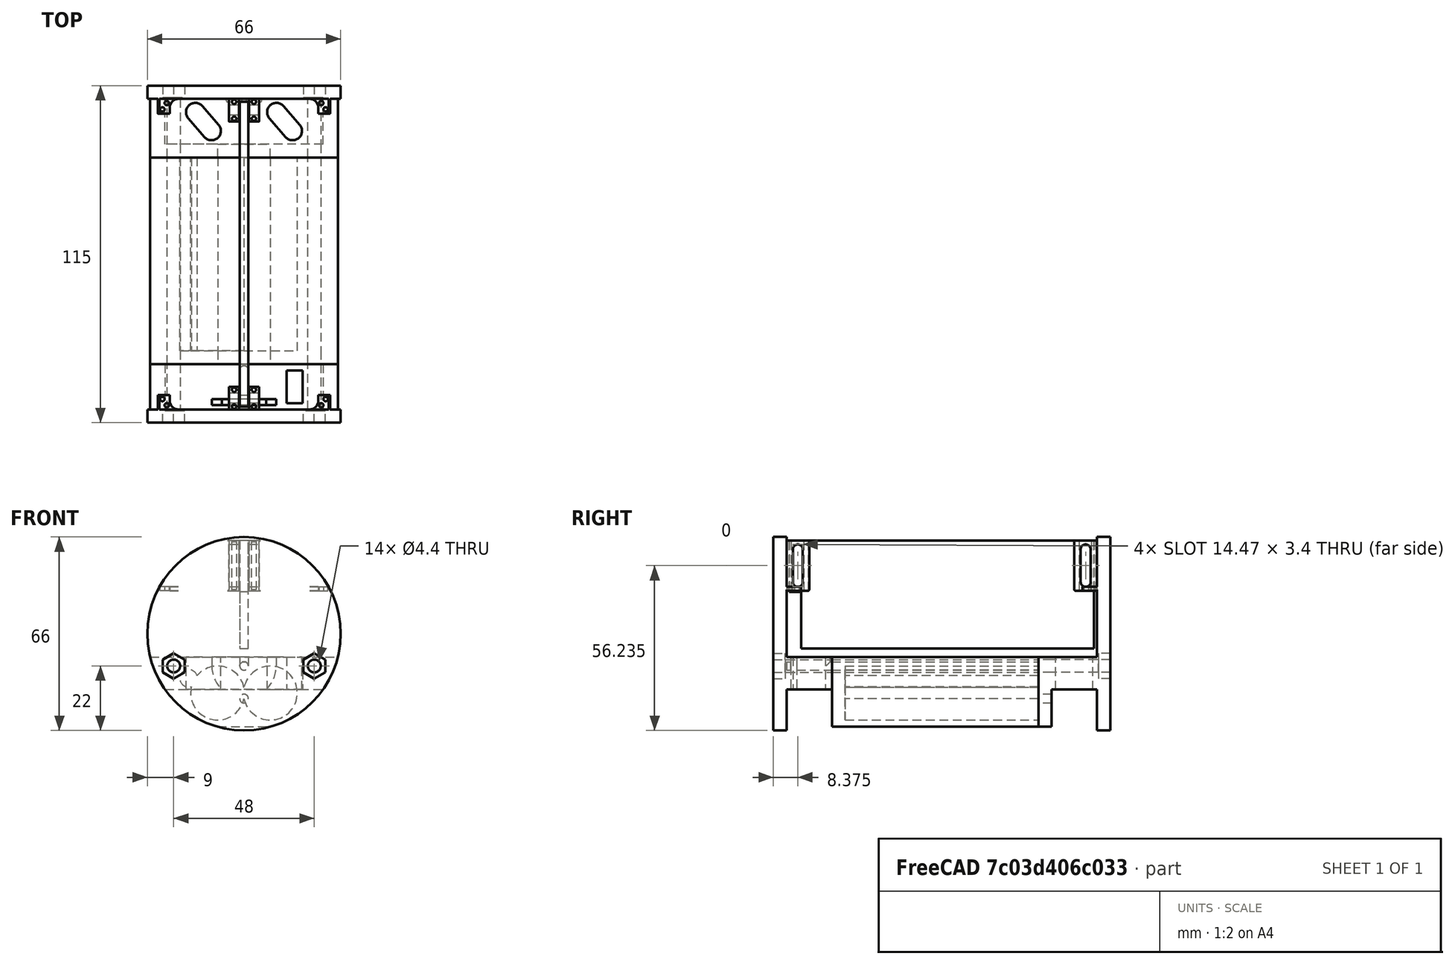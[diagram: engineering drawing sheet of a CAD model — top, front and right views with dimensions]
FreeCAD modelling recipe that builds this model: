
FCSTD DOCUMENT  (FreeCAD 0.19R24276 (Git))
Label: Corte_piezas4
License: Creative Commons Attribution-ShareAlike
LicenseURL: http://creativecommons.org/licenses/by-sa/4.0/
objects: Sketcher::SketchObject×21, PartDesign::Pocket×11, PartDesign::Pad×10, PartDesign::Mirrored×7, PartDesign::Fillet×6, PartDesign::Body×4, PartDesign::ShapeBinder×4, PartDesign::MultiTransform×3, Spreadsheet::Sheet×1, TechDraw::DrawSVGTemplate×1, TechDraw::DrawViewPart×1, TechDraw::DrawViewDimension×1, TechDraw::DrawPage×1
note: 93 computed .brp shape members not serialized (recipe doc carries the construction recipe); baked Part::Feature solids carry a one-line shape summary decoded from their .brp

FEATURE [Spreadsheet::Sheet] Spreadsheet  label="Datos"
  cells = A1=Diámetro pila; B1(DiametroPila)=18; A2=Tolerancia; B2(tolerancia)=0.4; A3=Largo Pila; B3(largoPila)=65; A4=Separacion; B4(separacion)=1; A5=Grosor tapa; B5(grosortapa)=4.5; A6=Largo Bote; B6(LargoBote)=115; A7= Rosca pasante Diámetro; B7(roscaPasante4)=4; A8=Ancho placa electrónica; B8(anchoPlaca)=3; A9=Diámetro tornillos placa; B9(tornillosParaLaPlaca)=3
FEATURE [Sketcher::SketchObject] Sketch  label="habitaculo_pila_antena"
  FullyConstrained = true
  MapMode = 5
  Placement = pos=(0,0,0) rot=(1,0,0;1.5708rad)
  Support = -> [XZ_Plane]
  expr: Constraints[15] = <<Datos>>.DiametroPila
  expr: Constraints[2] = <<Datos>>.DiametroPila + <<Datos>>.tolerancia
  expr: Constraints[7] = <<Datos>>.tolerancia + <<Datos>>.roscaPasante4
  expr: Constraints[19] = 24
  sketch-geometry (13):
    g0: Circle CenterX=0 CenterY=0 CenterZ=0 NormalX=0 NormalY=0 NormalZ=1 AngleXU=0 Radius=33
    g1: LineSegment StartX=-9 StartY=-31.749 StartZ=0 EndX=9 EndY=-31.749 EndZ=0
    g2: LineSegment StartX=-32.0156 StartY=-8 StartZ=0 EndX=32.0156 EndY=-8 EndZ=0
    g3: ArcOfCircle CenterX=-9 CenterY=-20.249 CenterZ=0 NormalX=0 NormalY=0 NormalZ=1 AngleXU=0 Radius=9.2 StartAngle=0.208894 EndAngle=2.4418
    g4: ArcOfCircle CenterX=9 CenterY=-20.249 CenterZ=0 NormalX=0 NormalY=0 NormalZ=1 AngleXU=0 Radius=9.2 StartAngle=3.35049 EndAngle=9.21588
    g5: Circle CenterX=24 CenterY=-11 CenterZ=0 NormalX=0 NormalY=0 NormalZ=1 AngleXU=0 Radius=2.2
    g6: ArcOfCircle CenterX=0 CenterY=0 CenterZ=0 NormalX=0 NormalY=0 NormalZ=1 AngleXU=0 Radius=33 StartAngle=3.38646 EndAngle=4.43616
    g7: ArcOfCircle CenterX=0 CenterY=0 CenterZ=0 NormalX=0 NormalY=0 NormalZ=1 AngleXU=0 Radius=33 StartAngle=4.98862 EndAngle=6.03832
    g8: ArcOfCircle CenterX=-18.8935 CenterY=-15.243 CenterZ=0 NormalX=0 NormalY=0 NormalZ=1 AngleXU=0 Radius=3 StartAngle=0.311443 EndAngle=5.03488
    g9: ArcOfCircle CenterX=-9 CenterY=-20.249 CenterZ=0 NormalX=0 NormalY=0 NormalZ=1 AngleXU=0 Radius=9.2 StartAngle=2.90452 EndAngle=6.07429
    g10: Circle CenterX=-24 CenterY=-11 CenterZ=0 NormalX=0 NormalY=0 NormalZ=1 AngleXU=0 Radius=2.2
    g11: Circle CenterX=0 CenterY=-11 CenterZ=0 NormalX=0 NormalY=0 NormalZ=1 AngleXU=0 Radius=1.45
    g12: LineSegment StartX=24 StartY=-11 StartZ=0 EndX=0 EndY=-11 EndZ=0
  constraints (38):
    c: Diameter(g0) = 66
    c: Horizontal(g1)
    c: Diameter(g3) = 18.4
    c: Equal(g3,g4)
    c: Coincident(g4,g9)
    c: Coincident(g4,g3)
    c: Coincident(g0,g-1)
    c: Diameter(g5) = 4.4
    c: Horizontal(g2)
    c: Vertical(g1,g4)
    c: Coincident(g6,g-1)
    c: Coincident(g6,g1)
    c: Coincident(g7,g6)
    c: Coincident(g7,g1)
    c: Symmetric(g4,g3,g-2)
    c: DistanceX(g3,g4) = 18
    c: PointOnObject(g1,g0)
    c: DistanceY(g1,g3) = 11.5
    c: DistanceY(g5,g2) = 3
    c: DistanceX(g6,g5) = 24
    c: DistanceY(g2,g6) = 8
    c: PointOnObject(g6,g0)
    c: Coincident(g2,g6)
    c: Coincident(g7,g2)
    c: Equal(g3,g9)
    c: Coincident(g3,g8)
    c: Coincident(g9,g8)
    c: Coincident(g3,g9)
    c: Radius(g8) = 3
    c: DistanceX(g8,g2) = -13.1222
    c: DistanceY(g8,g2) = 7.24297
    c: Symmetric(g10,g5,g-2)
    c: Equal(g10,g5)
    c: Diameter(g11) = 2.9  'Antena'
    c: Coincident(g12,g5)
    c: Coincident(g12,g11)
    c: Horizontal(g12)
    c: PointOnObject(g11,g-2)
FEATURE [PartDesign::Pad] Pad  label="habitaculo_Pila"
  Direction = (1,1,1)
  Length = 66
  Length2 = 100
  Midplane = true
  Placement = pos=(0,0,0) rot=(1,0,0;1.5708rad)
  Profile = -> Sketch
  Type = 0
  expr: Length = <<Datos>>.largoPila + <<Datos>>.separacion
FEATURE [Sketcher::SketchObject] Sketch001  label="TapaHabitaculoSK"
  ExternalGeometry = -> [Pad]
  FullyConstrained = true
  MapMode = 5
  Placement = pos=(0,-33,-7.3e-15) rot=(1,0,0;1.5708rad)
  Support = -> [Pad]
  sketch-geometry (7):
    g0: ArcOfCircle CenterX=0 CenterY=-5.4e-15 CenterZ=0 NormalX=0 NormalY=0 NormalZ=1 AngleXU=0 Radius=33 StartAngle=3.38646 EndAngle=4.43616
    g1: ArcOfCircle CenterX=0 CenterY=-5.4e-15 CenterZ=0 NormalX=0 NormalY=0 NormalZ=1 AngleXU=0 Radius=33 StartAngle=4.98862 EndAngle=6.03832
    g2: LineSegment StartX=-32.0156 StartY=-8 StartZ=0 EndX=32.0156 EndY=-8 EndZ=0
    g3: LineSegment StartX=-9 StartY=-31.749 StartZ=0 EndX=9 EndY=-31.749 EndZ=0
    g4: Circle CenterX=-24 CenterY=-11 CenterZ=0 NormalX=0 NormalY=0 NormalZ=1 AngleXU=0 Radius=2.2
    g5: Circle CenterX=0 CenterY=-11 CenterZ=0 NormalX=0 NormalY=0 NormalZ=1 AngleXU=0 Radius=1.45
    g6: Circle CenterX=24 CenterY=-11 CenterZ=0 NormalX=0 NormalY=0 NormalZ=1 AngleXU=0 Radius=2.2
  constraints (15):
    c: Coincident(g0,g-3)
    c: Coincident(g0,g-3)
    c: Coincident(g1,g0)
    c: Coincident(g1,g-4)
    c: Coincident(g1,g-4)
    c: Coincident(g2,g0)
    c: Coincident(g2,g1)
    c: Coincident(g3,g0)
    c: Coincident(g3,g1)
    c: Coincident(g4,g-6)
    c: PointOnObject(g-5,g4)
    c: Coincident(g5,g-7)
    c: Coincident(g6,g-8)
    c: Equal(g6,g-8)
    c: Equal(g5,g-7)
FEATURE [PartDesign::Pad] Pad001  label="TapaHabitaculoPilas"
  BaseFeature = -> Pad
  Direction = (1,1,1)
  Length = 4.5
  Length2 = 100
  Placement = pos=(0,0,0) rot=(1,0,0;1.5708rad)
  Profile = -> Sketch001
  Type = 0
  expr: Length = <<Datos>>.grosortapa
FEATURE [PartDesign::Body] Body  label="Habitaculo_Pila"
  Group = -> [Sketch,Pad,Sketch001,Pad001]
  Origin = -> Origin
  Tip = -> Pad001
FEATURE [PartDesign::ShapeBinder] ShapeBinder  label="LateralA_SB"
  Placement = pos=(0,-4.5,-1e-15) rot=(0,0,1;0rad)
  Support = -> [Pad001]
  TraceSupport = false
FEATURE [Sketcher::SketchObject] Sketch002  label="LateralA_SK"
  ExternalGeometry = -> [ShapeBinder]
  FullyConstrained = true
  MapMode = 5
  Placement = pos=(0,-37.5,-1.19e-14) rot=(1,0,0;1.5708rad)
  Support = -> [ShapeBinder]
  sketch-geometry (9):
    g0: LineSegment StartX=-32.0156 StartY=-8 StartZ=0 EndX=32.0156 EndY=-8 EndZ=0
    g1: LineSegment StartX=-26.96 StartY=-19.0305 StartZ=0 EndX=26.96 EndY=-19.0305 EndZ=0
    g2: ArcOfCircle CenterX=0 CenterY=0 CenterZ=0 NormalX=0 NormalY=0 NormalZ=1 AngleXU=0 Radius=33 StartAngle=3.38646 EndAngle=3.75625
    g3: ArcOfCircle CenterX=0 CenterY=0 CenterZ=0 NormalX=0 NormalY=0 NormalZ=1 AngleXU=0 Radius=33 StartAngle=5.66852 EndAngle=6.03832
    g4: Circle CenterX=24 CenterY=-11 CenterZ=0 NormalX=0 NormalY=0 NormalZ=1 AngleXU=0 Radius=2.2
    g5: Circle CenterX=0 CenterY=-11 CenterZ=0 NormalX=0 NormalY=0 NormalZ=1 AngleXU=0 Radius=1.45
    g6: Circle CenterX=-24 CenterY=-11 CenterZ=0 NormalX=0 NormalY=0 NormalZ=1 AngleXU=0 Radius=2.2
    g7: LineSegment StartX=-32.0156 StartY=-8 StartZ=0 EndX=-24 EndY=-11 EndZ=0
    g8: LineSegment StartX=-24 StartY=-11 StartZ=0 EndX=-26.96 EndY=-19.0305 EndZ=0
  constraints (20):
    c: Coincident(g0,g-3)
    c: Coincident(g0,g-4)
    c: Horizontal(g1)
    c: Coincident(g2,g-1)
    c: Coincident(g2,g0)
    c: Coincident(g2,g1)
    c: Coincident(g3,g2)
    c: Coincident(g3,g0)
    c: Coincident(g3,g1)
    c: Coincident(g4,g-7)
    c: Coincident(g5,g-6)
    c: Coincident(g6,g-5)
    c: Equal(g4,g-7)
    c: Equal(g5,g-6)
    c: Equal(g6,g-5)
    c: Coincident(g7,g0)
    c: Coincident(g7,g6)
    c: Coincident(g8,g1)
    c: Equal(g7,g8)
    c: Coincident(g8,g6)
FEATURE [PartDesign::Pad] Pad002  label="lateralA"
  Direction = (1,1,1)
  Length = 15.5
  Length2 = 100
  Placement = pos=(0,-4.5,-1e-15) rot=(0,0,1;0rad)
  Profile = -> Sketch002
  Type = 0
  expr: Length = <<Datos>>.LargoBote / 2 - 2 * <<Datos>>.grosortapa - (<<Datos>>.largoPila + <<Datos>>.separacion) / 2
FEATURE [Sketcher::SketchObject] Sketch003  label="tapaLateralASK"
  ExternalGeometry = -> [Pad002]
  FullyConstrained = true
  MapMode = 5
  Placement = pos=(0,-53,-3.16e-14) rot=(1,0,0;1.5708rad)
  Support = -> [Pad002]
  sketch-geometry (3):
    g0: Circle CenterX=0 CenterY=0 CenterZ=0 NormalX=0 NormalY=0 NormalZ=1 AngleXU=0 Radius=33
    g1: Circle CenterX=24 CenterY=-11 CenterZ=0 NormalX=0 NormalY=0 NormalZ=1 AngleXU=0 Radius=2.2
    g2: Circle CenterX=-24 CenterY=-11 CenterZ=0 NormalX=0 NormalY=0 NormalZ=1 AngleXU=0 Radius=2.2
  constraints (7):
    c: Coincident(g0,g-1)
    c: PointOnObject(g-3,g0)
    c: Diameter(g-6) = 4.4
    c: Coincident(g1,g-6)
    c: Equal(g1,g-6)
    c: Coincident(g2,g-5)
    c: Equal(g2,g-5)
FEATURE [PartDesign::Pad] Pad003  label="TapaLateralA"
  BaseFeature = -> Pad002
  Direction = (1,1,1)
  Length = 4.5
  Length2 = 100
  Placement = pos=(0,-4.5,-1e-15) rot=(0,0,1;0rad)
  Profile = -> Sketch003
  Type = 0
  expr: Length = <<Datos>>.grosortapa
FEATURE [PartDesign::ShapeBinder] ShapeBinder001  label="LateralB_SB"
  Placement = pos=(0,33,7e-15) rot=(0,0,1;0rad)
  Support = -> [Pad001]
  TraceSupport = false
FEATURE [Sketcher::SketchObject] Sketch004  label="LateralBSK"
  ExternalGeometry = -> [ShapeBinder001]
  FullyConstrained = true
  MapMode = 5
  Placement = pos=(0,33,7e-15) rot=(0,0.707107,0.707107;3.14159rad)
  Support = -> [ShapeBinder001]
  sketch-geometry (6):
    g0: ArcOfCircle CenterX=3.5e-15 CenterY=-2.7e-15 CenterZ=0 NormalX=0 NormalY=0 NormalZ=1 AngleXU=0 Radius=33 StartAngle=3.38646 EndAngle=4.43616
    g1: ArcOfCircle CenterX=3.5e-15 CenterY=-2.7e-15 CenterZ=0 NormalX=0 NormalY=0 NormalZ=1 AngleXU=0 Radius=33 StartAngle=4.98862 EndAngle=6.03832
    g2: LineSegment StartX=-32.0156 StartY=-8 StartZ=0 EndX=32.0156 EndY=-8 EndZ=0
    g3: LineSegment StartX=9 StartY=-31.749 StartZ=0 EndX=-9 EndY=-31.749 EndZ=0
    g4: Circle CenterX=24 CenterY=-11 CenterZ=0 NormalX=0 NormalY=0 NormalZ=1 AngleXU=0 Radius=2.2
    g5: Circle CenterX=-24 CenterY=-11 CenterZ=0 NormalX=0 NormalY=0 NormalZ=1 AngleXU=0 Radius=2.2
  constraints (13):
    c: Coincident(g0,g-3)
    c: Coincident(g1,g0)
    c: Coincident(g1,g-4)
    c: Coincident(g1,g-4)
    c: Coincident(g-3,g0)
    c: Coincident(g2,g0)
    c: Coincident(g2,g1)
    c: Coincident(g3,g1)
    c: Coincident(g3,g0)
    c: Coincident(g4,g-6)
    c: Equal(g4,g-6)
    c: Coincident(g5,g-5)
    c: Equal(g5,g-5)
FEATURE [PartDesign::Pad] Pad004  label="TaparPilaLateralB"
  Direction = (1,1,1)
  Length = 4.5
  Length2 = 100
  Placement = pos=(0,33,7e-15) rot=(0,0,1;0rad)
  Profile = -> Sketch004
  Type = 0
  expr: Length = <<Datos>>.grosortapa
FEATURE [Sketcher::SketchObject] Sketch005  label="LateralBProlongacionSK"
  ExternalGeometry = -> [Pad004]
  FullyConstrained = true
  MapMode = 5
  Placement = pos=(0,37.5,8.5e-15) rot=(0,0.707107,0.707107;3.14159rad)
  Support = -> [Pad004]
  sketch-geometry (8):
    g0: ArcOfCircle CenterX=0 CenterY=0 CenterZ=0 NormalX=0 NormalY=0 NormalZ=1 AngleXU=0 Radius=33 StartAngle=3.38646 EndAngle=3.75625
    g1: ArcOfCircle CenterX=0 CenterY=0 CenterZ=0 NormalX=0 NormalY=0 NormalZ=1 AngleXU=0 Radius=33 StartAngle=5.66852 EndAngle=6.03832
    g2: LineSegment StartX=-26.96 StartY=-19.0305 StartZ=0 EndX=26.96 EndY=-19.0305 EndZ=0
    g3: LineSegment StartX=32.0156 StartY=-8 StartZ=0 EndX=-32.0156 EndY=-8 EndZ=0
    g4: Circle CenterX=-24 CenterY=-11 CenterZ=0 NormalX=0 NormalY=0 NormalZ=1 AngleXU=0 Radius=2.2
    g5: Circle CenterX=24 CenterY=-11 CenterZ=0 NormalX=0 NormalY=0 NormalZ=1 AngleXU=0 Radius=2.2
    g6: LineSegment StartX=-32.0156 StartY=-8 StartZ=0 EndX=-24 EndY=-11 EndZ=0
    g7: LineSegment StartX=-26.96 StartY=-19.0305 StartZ=0 EndX=-24 EndY=-11 EndZ=0
  constraints (18):
    c: Coincident(g0,g-1)
    c: Coincident(g0,g-3)
    c: Coincident(g1,g0)
    c: Coincident(g1,g-4)
    c: Coincident(g2,g0)
    c: Coincident(g2,g1)
    c: Horizontal(g2)
    c: Coincident(g3,g1)
    c: Coincident(g3,g0)
    c: Coincident(g4,g-5)
    c: Coincident(g5,g-6)
    c: Equal(g5,g-6)
    c: Equal(g4,g-5)
    c: Coincident(g6,g0)
    c: Coincident(g6,g4)
    c: Coincident(g7,g0)
    c: Coincident(g7,g4)
    c: Equal(g6,g7)
FEATURE [PartDesign::Pad] Pad005  label="LateralBProlongacion"
  BaseFeature = -> Pad004
  Direction = (1,1,1)
  Length = 15.5
  Length2 = 100
  Placement = pos=(0,33,7e-15) rot=(0,0,1;0rad)
  Profile = -> Sketch005
  Type = 0
  expr: Length = <<lateralA>>.Length
FEATURE [Sketcher::SketchObject] Sketch006  label="TapaLateralB_SK"
  ExternalGeometry = -> [Pad005]
  FullyConstrained = true
  MapMode = 5
  Placement = pos=(0,53,1.96e-14) rot=(0,0.707107,0.707107;3.14159rad)
  Support = -> [Pad005]
  sketch-geometry (3):
    g0: Circle CenterX=0 CenterY=0 CenterZ=0 NormalX=0 NormalY=0 NormalZ=1 AngleXU=0 Radius=33
    g1: Circle CenterX=-24 CenterY=-11 CenterZ=0 NormalX=0 NormalY=0 NormalZ=1 AngleXU=0 Radius=2.2
    g2: Circle CenterX=24 CenterY=-11 CenterZ=0 NormalX=0 NormalY=0 NormalZ=1 AngleXU=0 Radius=2.2
  constraints (6):
    c: Coincident(g0,g-1)
    c: PointOnObject(g-3,g0)
    c: Coincident(g1,g-4)
    c: Coincident(g2,g-6)
    c: Equal(g2,g-6)
    c: Equal(g-4,g1)
FEATURE [PartDesign::Pad] Pad006  label="TapaLateralB"
  BaseFeature = -> Pad005
  Direction = (1,1,1)
  Length = 4.5
  Length2 = 100
  Placement = pos=(0,33,7e-15) rot=(0,0,1;0rad)
  Profile = -> Sketch006
  Type = 0
  expr: Length = <<Datos>>.grosortapa
FEATURE [Sketcher::SketchObject] Sketch007  label="Ranura_AntenaSK"
  ExternalGeometry = -> [Pad003]
  FullyConstrained = true
  MapMode = 5
  Placement = pos=(-1.4e-15,-4.5,-8) rot=(0,0,1;0rad)
  Support = -> [Pad003]
  sketch-geometry (5):
    g0: ArcOfCircle CenterX=0 CenterY=-35 CenterZ=0 NormalX=0 NormalY=0 NormalZ=1 AngleXU=0 Radius=1.45 StartAngle=-1.199e-12 EndAngle=3.14159
    g1: LineSegment StartX=-1.45 StartY=-35 StartZ=0 EndX=-1.45 EndY=-45 EndZ=0
    g2: LineSegment StartX=1.45 StartY=-35 StartZ=0 EndX=1.45 EndY=-45 EndZ=0
    g3: LineSegment StartX=-1.45 StartY=-45 StartZ=0 EndX=1.45 EndY=-45 EndZ=0
    g4: LineSegment StartX=32.0156 StartY=-48.5 StartZ=0 EndX=0 EndY=-33 EndZ=0
  constraints (14):
    c: Tangent(g0,g2) = 1.5708
    c: Tangent(g0,g1) = -1.5708
    c: Vertical(g1)
    c: Coincident(g3,g1)
    c: Coincident(g3,g2)
    c: Horizontal(g3)
    c: Parallel(g2,g1)
    c: Diameter(g0) = 2.9
    c: DistanceY(g2,g2) = 10
    c: Coincident(g4,g-4)
    c: PointOnObject(g4,g-2)
    c: PointOnObject(g4,g-3)
    c: DistanceY(g0,g-3) = 2
    c: PointOnObject(g0,g-2)
FEATURE [PartDesign::Pocket] Pocket  label="ConRanuraAntena"
  BaseFeature = -> Pad003
  Length = 3
  Length2 = 100
  Placement = pos=(0,-4.5,-1e-15) rot=(0,0,1;0rad)
  Profile = -> Sketch007
  Type = 0
FEATURE [Sketcher::SketchObject] Sketch008  label="Con_tuercas_sketch"
  FullyConstrained = false
  MapMode = 5
  Placement = pos=(0,-57.5,-4.07e-14) rot=(1,0,0;1.5708rad)
  Support = -> [Pocket]
  expr: Constraints[19] = 7 + <<Datos>>.tolerancia
  sketch-geometry (16):
    g0: LineSegment StartX=27.7 StartY=-13.1362 StartZ=0 EndX=27.7 EndY=-8.8638 EndZ=0
    g1: LineSegment StartX=27.7 StartY=-8.8638 StartZ=0 EndX=24 EndY=-6.72761 EndZ=0
    g2: LineSegment StartX=24 StartY=-6.72761 StartZ=0 EndX=20.3 EndY=-8.8638 EndZ=0
    g3: LineSegment StartX=20.3 StartY=-8.8638 StartZ=0 EndX=20.3 EndY=-13.1362 EndZ=0
    g4: LineSegment StartX=20.3 StartY=-13.1362 StartZ=0 EndX=24 EndY=-15.2724 EndZ=0
    g5: LineSegment StartX=24 StartY=-15.2724 StartZ=0 EndX=27.7 EndY=-13.1362 EndZ=0
    g6: Circle CenterX=24 CenterY=-11 CenterZ=0 NormalX=0 NormalY=0 NormalZ=1 AngleXU=0 Radius=4.27239
    g7: LineSegment StartX=20.3 StartY=-8.8638 StartZ=0 EndX=27.7 EndY=-8.8638 EndZ=0
    g8: LineSegment StartX=-20.3 StartY=-13.1362 StartZ=0 EndX=-20.3 EndY=-8.8638 EndZ=0
    g9: LineSegment StartX=-20.3 StartY=-8.8638 StartZ=0 EndX=-24 EndY=-6.72761 EndZ=0
    g10: LineSegment StartX=-24 StartY=-6.72761 StartZ=0 EndX=-27.7 EndY=-8.8638 EndZ=0
    g11: LineSegment StartX=-27.7 StartY=-8.8638 StartZ=0 EndX=-27.7 EndY=-13.1362 EndZ=0
    g12: LineSegment StartX=-27.7 StartY=-13.1362 StartZ=0 EndX=-24 EndY=-15.2724 EndZ=0
    g13: LineSegment StartX=-24 StartY=-15.2724 StartZ=0 EndX=-20.3 EndY=-13.1362 EndZ=0
    g14: Circle CenterX=-24 CenterY=-11 CenterZ=0 NormalX=0 NormalY=0 NormalZ=1 AngleXU=0 Radius=4.27239
    g15: LineSegment StartX=-27.7 StartY=-8.8638 StartZ=0 EndX=-20.3 EndY=-8.8638 EndZ=0
  constraints (34):
    c: Coincident(g0,g1)
    c: Coincident(g1,g2)
    c: Coincident(g2,g3)
    c: Coincident(g3,g4)
    c: Coincident(g4,g5)
    c: Coincident(g5,g0)
    c: Equal(g0, g1-g5) x5
    c: PointOnObject(g0,g6)
    c: PointOnObject(g1,g6)
    c: PointOnObject(g2,g6)
    c: PointOnObject(g3,g6)
    c: PointOnObject(g4,g6)
    c: PointOnObject(g5,g6)
    c: Coincident(g7,g2)
    c: Coincident(g7,g0)
    c: Distance(g7) = 7.4
    c: Vertical(g0)
    c: Coincident(g8,g9)
    c: Coincident(g9,g10)
    c: Coincident(g10,g11)
    c: Coincident(g11,g12)
    c: Coincident(g12,g13)
    c: Coincident(g13,g8)
    c: Equal(g8, g9-g13) x5
    c: PointOnObject(g8,g14)
    c: PointOnObject(g9,g14)
    c: PointOnObject(g10,g14)
    c: PointOnObject(g11,g14)
    c: PointOnObject(g12,g14)
    c: PointOnObject(g13,g14)
    c: Coincident(g15,g10)
    c: Coincident(g15,g8)
    c: Distance(g15) = 7.4
    c: Vertical(g8)
FEATURE [PartDesign::Pocket] Pocket001  label="Con_tuercas"
  BaseFeature = -> Pocket
  Length = 4
  Length2 = 100
  Placement = pos=(0,-4.5,-1e-15) rot=(0,0,1;0rad)
  Profile = -> Sketch008
  Type = 0
FEATURE [PartDesign::ShapeBinder] ShapeBinder002  label="SB_Tuercas"
  Placement = pos=(0,-4.5,-1e-15) rot=(0,0,1;0rad)
  Support = -> [Pocket001]
  TraceSupport = false
FEATURE [Sketcher::SketchObject] Sketch009  label="Con_Tuercas"
  ExternalGeometry = -> [ShapeBinder002,Pad006]
  FullyConstrained = true
  MapMode = 5
  Placement = pos=(0,57.5,2.54e-14) rot=(0,0.707107,0.707107;3.14159rad)
  Support = -> [Pad006]
  sketch-geometry (14):
    g0: LineSegment StartX=24 StartY=-6.72761 StartZ=0 EndX=20.3 EndY=-8.8638 EndZ=0
    g1: LineSegment StartX=20.3 StartY=-8.8638 StartZ=0 EndX=20.3 EndY=-13.1362 EndZ=0
    g2: LineSegment StartX=20.3 StartY=-13.1362 StartZ=0 EndX=24 EndY=-15.2724 EndZ=0
    g3: LineSegment StartX=24 StartY=-15.2724 StartZ=0 EndX=27.7 EndY=-13.1362 EndZ=0
    g4: LineSegment StartX=27.7 StartY=-13.1362 StartZ=0 EndX=27.7 EndY=-8.8638 EndZ=0
    g5: LineSegment StartX=27.7 StartY=-8.8638 StartZ=0 EndX=24 EndY=-6.72761 EndZ=0
    g6: Circle CenterX=24 CenterY=-11 CenterZ=0 NormalX=0 NormalY=0 NormalZ=1 AngleXU=0 Radius=4.27239
    g7: LineSegment StartX=-24 StartY=-6.72761 StartZ=0 EndX=-27.7 EndY=-8.8638 EndZ=0
    g8: LineSegment StartX=-27.7 StartY=-8.8638 StartZ=0 EndX=-27.7 EndY=-13.1362 EndZ=0
    g9: LineSegment StartX=-27.7 StartY=-13.1362 StartZ=0 EndX=-24 EndY=-15.2724 EndZ=0
    g10: LineSegment StartX=-24 StartY=-15.2724 StartZ=0 EndX=-20.3 EndY=-13.1362 EndZ=0
    g11: LineSegment StartX=-20.3 StartY=-13.1362 StartZ=0 EndX=-20.3 EndY=-8.8638 EndZ=0
    g12: LineSegment StartX=-20.3 StartY=-8.8638 StartZ=0 EndX=-24 EndY=-6.72761 EndZ=0
    g13: Circle CenterX=-24 CenterY=-11 CenterZ=0 NormalX=0 NormalY=0 NormalZ=1 AngleXU=0 Radius=4.27239
  constraints (30):
    c: Coincident(g0,g1)
    c: Coincident(g1,g2)
    c: Coincident(g2,g3)
    c: Coincident(g3,g4)
    c: Coincident(g4,g5)
    c: Coincident(g5,g0)
    c: Equal(g0, g1-g5) x5
    c: PointOnObject(g0,g6)
    c: PointOnObject(g1,g6)
    c: PointOnObject(g2,g6)
    c: PointOnObject(g3,g6)
    c: PointOnObject(g4,g6)
    c: PointOnObject(g5,g6)
    c: Coincident(g6,g-4)
    c: Coincident(g5,g-3)
    c: Coincident(g7,g8)
    c: Coincident(g8,g9)
    c: Coincident(g9,g10)
    c: Coincident(g10,g11)
    c: Coincident(g11,g12)
    c: Coincident(g12,g7)
    c: Equal(g7, g8-g12) x5
    c: PointOnObject(g7,g13)
    c: PointOnObject(g8,g13)
    c: PointOnObject(g9,g13)
    c: PointOnObject(g10,g13)
    c: PointOnObject(g11,g13)
    c: PointOnObject(g12,g13)
    c: Coincident(g13,g-5)
    c: Coincident(g12,g-6)
FEATURE [PartDesign::Pocket] Pocket002  label="Tapa_lateral_B_con_tuercas"
  BaseFeature = -> Pad006
  Length = 4
  Length2 = 100
  Placement = pos=(0,33,7e-15) rot=(0,0,1;0rad)
  Profile = -> Sketch009
  Type = 0
FEATURE [Sketcher::SketchObject] Sketch010  label="ArandelaSK"
  ExternalGeometry = -> [Pocket001]
  FullyConstrained = true
  MapMode = 5
  Placement = pos=(0,-49.5,-1.09e-14) rot=(0,0.707107,0.707107;3.14159rad)
  Support = -> [Pocket001]
  sketch-geometry (6):
    g0: ArcOfCircle CenterX=0 CenterY=-11 CenterZ=0 NormalX=0 NormalY=0 NormalZ=1 AngleXU=0 Radius=11 StartAngle=3.14159 EndAngle=6.28319
    g1: LineSegment StartX=-11 StartY=0 StartZ=0 EndX=11 EndY=0 EndZ=0
    g2: LineSegment StartX=-11 StartY=0 StartZ=0 EndX=-11 EndY=-11 EndZ=0
    g3: LineSegment StartX=11 StartY=0 StartZ=0 EndX=11 EndY=-11 EndZ=0
    g4: Circle CenterX=0 CenterY=-11 CenterZ=0 NormalX=0 NormalY=0 NormalZ=1 AngleXU=0 Radius=11
    g5: Circle CenterX=0 CenterY=11 CenterZ=0 NormalX=0 NormalY=0 NormalZ=1 AngleXU=0 Radius=11
  constraints (15):
    c: Coincident(g0,g-3)
    c: PointOnObject(g-1,g0)
    c: Horizontal(g1)
    c: PointOnObject(g-1,g1)
    c: Coincident(g2,g1)
    c: Vertical(g3)
    c: Coincident(g1,g3)
    c: Vertical(g2)
    c: Tangent(g0,g2) = -1.5708
    c: Tangent(g0,g3) = 1.5708
    c: Coincident(g4,g0)
    c: PointOnObject(g0,g4)
    c: PointOnObject(g5,g-2)
    c: Equal(g4,g5)
    c: Tangent(g5,g4)
FEATURE [PartDesign::Pocket] Pocket003  label="Arandela_plano_GND"
  BaseFeature = -> Pocket001
  Length = 2
  Length2 = 100
  Placement = pos=(0,-4.5,-1e-15) rot=(0,0,1;0rad)
  Profile = -> Sketch010
  Type = 0
FEATURE [TechDraw::DrawSVGTemplate] Template
  EditableTexts = Designed_by_Name=Designed by Name; Drawing_number=Drawing number; FC-Date=Date; FC-SC=Scale; FC-SH=Sheet; FC-Title=Title; Subtitle=Subtitle; Weight=Weight
  Height = 210
  Orientation = 1
  Width = 297
FEATURE [Sketcher::SketchObject] Sketch011  label="Pasacables_RFM69"
  ExternalGeometry = -> [Pocket003]
  FullyConstrained = true
  MapMode = 5
  Placement = pos=(-1.4e-15,-4.5,-8) rot=(0,0,1;0rad)
  Support = -> [Pocket003]
  sketch-geometry (4):
    g0: LineSegment StartX=14.5156 StartY=-35.2 StartZ=0 EndX=20.0156 EndY=-35.2 EndZ=0
    g1: LineSegment StartX=20.0156 StartY=-35.2 StartZ=0 EndX=20.0156 EndY=-46.3 EndZ=0
    g2: LineSegment StartX=20.0156 StartY=-46.3 StartZ=0 EndX=14.5156 EndY=-46.3 EndZ=0
    g3: LineSegment StartX=14.5156 StartY=-46.3 StartZ=0 EndX=14.5156 EndY=-35.2 EndZ=0
  constraints (12):
    c: Coincident(g0,g1)
    c: Coincident(g1,g2)
    c: Coincident(g2,g3)
    c: Coincident(g3,g0)
    c: Horizontal(g0)
    c: Horizontal(g2)
    c: Vertical(g1)
    c: Vertical(g3)
    c: DistanceX(g0,g-4) = 12
    c: DistanceY(g0,g-4) = 2.2
    c: DistanceY(g-4,g1) = 2.2
    c: DistanceX(g0,g0) = 5.5
FEATURE [PartDesign::Pocket] Pocket004  label="LateralA_Pasacables"
  BaseFeature = -> Pocket003
  Length = 5
  Length2 = 100
  Placement = pos=(0,-4.5,-1e-15) rot=(0,0,1;0rad)
  Profile = -> Sketch011
  Type = 1
FEATURE [Sketcher::SketchObject] Sketch012  label="RanurasPlaca"
  ExternalGeometry = -> [Pocket004]
  FullyConstrained = true
  MapMode = 5
  Placement = pos=(0,-53,-3.74e-14) rot=(0,0.707107,0.707107;3.14159rad)
  Support = -> [Pocket004]
  expr: Constraints[42] = 2 * <<Datos>>.tolerancia
  expr: Constraints[28] = 2 * <<Datos>>.tolerancia
  expr: Constraints[19] = <<Datos>>.anchoPlaca + <<Datos>>.tolerancia
  sketch-geometry (16):
    g0: LineSegment StartX=-5.1 StartY=31.7936 StartZ=0 EndX=-1.7 EndY=31.7936 EndZ=0
    g1: LineSegment StartX=-1.7 StartY=31.7936 StartZ=0 EndX=-1.7 EndY=14.677 EndZ=0
    g2: LineSegment StartX=-1.7 StartY=14.677 StartZ=0 EndX=-5.1 EndY=14.677 EndZ=0
    g3: LineSegment StartX=-5.1 StartY=14.677 StartZ=0 EndX=-5.1 EndY=31.7936 EndZ=0
    g4: LineSegment StartX=1.7 StartY=31.7936 StartZ=0 EndX=5.1 EndY=31.7936 EndZ=0
    g5: LineSegment StartX=5.1 StartY=31.7936 StartZ=0 EndX=5.1 EndY=14.677 EndZ=0
    g6: LineSegment StartX=5.1 StartY=14.677 StartZ=0 EndX=1.7 EndY=14.677 EndZ=0
    g7: LineSegment StartX=1.7 StartY=14.677 StartZ=0 EndX=1.7 EndY=31.7936 EndZ=0
    g8: LineSegment StartX=-1.7 StartY=31.7936 StartZ=0 EndX=1.7 EndY=31.7936 EndZ=0
    g9: LineSegment StartX=5.1 StartY=-8 StartZ=0 EndX=5.1 EndY=14.677 EndZ=0
    g10: LineSegment StartX=0 StartY=0 StartZ=0 EndX=5.22671 EndY=32.5835 EndZ=0
    g11: GeomPoint X=0 Y=3.00003 Z=0
    g12: Circle CenterX=0 CenterY=-10.9733 CenterZ=0 NormalX=0 NormalY=0 NormalZ=1 AngleXU=0 Radius=11
    g13: Circle CenterX=0 CenterY=3.00003 CenterZ=0 NormalX=0 NormalY=0 NormalZ=1 AngleXU=0 Radius=11
    g14: Circle CenterX=0 CenterY=3.00003 CenterZ=0 NormalX=0 NormalY=0 NormalZ=1 AngleXU=0 Radius=11.8
    g15: LineSegment StartX=0 StartY=14.0001 StartZ=0 EndX=0 EndY=14.8001 EndZ=0
  constraints (44):
    c: Coincident(g0,g1)
    c: Coincident(g1,g2)
    c: Coincident(g2,g3)
    c: Coincident(g3,g0)
    c: Horizontal(g0)
    c: Horizontal(g2)
    c: Vertical(g1)
    c: Vertical(g3)
    c: Coincident(g4,g5)
    c: Coincident(g5,g6)
    c: Coincident(g6,g7)
    c: Coincident(g7,g4)
    c: Horizontal(g4)
    c: Horizontal(g6)
    c: Vertical(g5)
    c: Vertical(g7)
    c: Symmetric(g4,g0,g-2)
    c: Equal(g7,g1)
    c: Equal(g6,g2)
    c: DistanceX(g0,g4) = 3.4
    c: Coincident(g8,g0)
    c: Coincident(g8,g4)
    c: PointOnObject(g9,g-3)
    c: Coincident(g9,g5)
    c: Vertical(g9)
    c: Coincident(g10,g-1)
    c: PointOnObject(g10,g-4)
    c: PointOnObject(g4,g10)
    c: Distance(g4,g10) = 0.8
    c: Equal(g8,g4)
    c: PointOnObject(g11,g-2)
    c: PointOnObject(g-5,g12)
    c: PointOnObject(g12,g-2)
    c: PointOnObject(g-6,g12)
    c: Coincident(g13,g11)
    c: Tangent(g13,g-3)
    c: Equal(g13,g12)
    c: Coincident(g14,g11)
    c: PointOnObject(g15,g13)
    c: PointOnObject(g15,g14)
    c: PointOnObject(g15,g-2)
    c: PointOnObject(g15,g-2)
    c: DistanceY(g15,g15) = 0.8
    c: PointOnObject(g6,g14)
FEATURE [PartDesign::Pad] Pad007  label="Ranura_Placa"
  BaseFeature = -> Pocket004
  Direction = (1,1,1)
  Length = 7.75
  Length2 = 100
  Placement = pos=(0,-4.5,-1e-15) rot=(0,0,1;0rad)
  Profile = -> Sketch012
  Type = 0
  expr: Length = <<lateralA>>.Length / 2
FEATURE [Sketcher::SketchObject] Sketch015  label="Agujero_cables_positivo_negativo"
  ExternalGeometry = -> [ShapeBinder001]
  FullyConstrained = true
  MapMode = 5
  Placement = pos=(0,33,7e-15) rot=(1,0,0;1.5708rad)
  Support = -> [Pocket002]
  sketch-geometry (1):
    g0: Circle CenterX=0 CenterY=-22.1569 CenterZ=0 NormalX=0 NormalY=0 NormalZ=1 AngleXU=0 Radius=1.5
  constraints (2):
    c: Coincident(g0,g-3)
    c: Radius(g0) = 1.5
FEATURE [PartDesign::Pocket] Pocket007  label="Agujero_sacar_cables"
  BaseFeature = -> Pocket002
  Length = 5
  Length2 = 100
  Placement = pos=(0,33,7e-15) rot=(0,0,1;0rad)
  Profile = -> Sketch015
  Type = 2
FEATURE [Sketcher::SketchObject] Sketch013  label="SoporteTornilloPlaca"
  ExternalGeometry = -> [Pad007]
  FullyConstrained = true
  MapMode = 5
  Placement = pos=(5.1,-4.5,-1e-15) rot=(0.57735,0.57735,0.57735;2.0944rad)
  Support = -> [Pad007]
  expr: Constraints[10] = <<Datos>>.tornillosParaLaPlaca + <<Datos>>.tolerancia
  sketch-geometry (8):
    g0: ArcOfCircle CenterX=-44.625 CenterY=28.7693 CenterZ=0 NormalX=0 NormalY=0 NormalZ=1 AngleXU=0 Radius=1.7 StartAngle=8e-16 EndAngle=3.14159
    g1: ArcOfCircle CenterX=-44.625 CenterY=17.7012 CenterZ=0 NormalX=0 NormalY=0 NormalZ=1 AngleXU=0 Radius=1.7 StartAngle=3.14159 EndAngle=6.28319
    g2: LineSegment StartX=-46.325 StartY=28.7693 StartZ=0 EndX=-46.325 EndY=17.7012 EndZ=0
    g3: LineSegment StartX=-42.925 StartY=28.7693 StartZ=0 EndX=-42.925 EndY=17.7012 EndZ=0
    g4: LineSegment StartX=-44.625 StartY=31.7936 StartZ=0 EndX=-44.625 EndY=14.677 EndZ=0
    g5: LineSegment StartX=-44.625 StartY=23.2353 StartZ=0 EndX=-40.75 EndY=23.2353 EndZ=0
    g6: LineSegment StartX=-44.625 StartY=28.7693 StartZ=0 EndX=-40.75 EndY=23.2353 EndZ=0
    g7: LineSegment StartX=-40.75 StartY=23.2353 StartZ=0 EndX=-44.625 EndY=17.7012 EndZ=0
  constraints (20):
    c: Tangent(g0,g3) = 1.5708
    c: Tangent(g0,g2) = -1.5708
    c: Tangent(g2,g1) = -1.5708
    c: Tangent(g3,g1) = 1.5708
    c: Vertical(g2)
    c: Equal(g0,g1)
    c: PointOnObject(g4,g-5)
    c: Symmetric(g-3,g-4,g4)
    c: Vertical(g4)
    c: PointOnObject(g0,g4)
    c: Diameter(g0) = 3.4
    c: PointOnObject(g5,g4)
    c: Horizontal(g5)
    c: Symmetric(g-4,g-5,g5)
    c: Coincident(g6,g0)
    c: Coincident(g6,g5)
    c: Coincident(g7,g5)
    c: Coincident(g7,g1)
    c: Angle(g4,g6) = 0.610865
    c: Angle(g7,g4) = 0.610865
FEATURE [PartDesign::Pocket] Pocket005  label="Tornillos_placa"
  BaseFeature = -> Pad007
  Length = 5
  Length2 = 100
  Placement = pos=(0,-4.5,-1e-15) rot=(0,0,1;0rad)
  Profile = -> Sketch013
  Type = 1
FEATURE [Sketcher::SketchObject] Sketch017  label="Ranuras_A_paracaidas"
  ExternalGeometry = -> [Pocket005]
  FullyConstrained = true
  MapMode = 5
  Placement = pos=(0,-4.5,31.7936) rot=(0,0,1;0rad)
  Support = -> [Pocket005]
  sketch-geometry (12):
    g0: Circle CenterX=-3.36795 CenterY=-41.75 CenterZ=0 NormalX=0 NormalY=0 NormalZ=1 AngleXU=0 Radius=0.75
    g1: Circle CenterX=3.36795 CenterY=-41.75 CenterZ=0 NormalX=0 NormalY=0 NormalZ=1 AngleXU=0 Radius=0.75
    g2: Circle CenterX=-3.36795 CenterY=-47.5 CenterZ=0 NormalX=0 NormalY=0 NormalZ=1 AngleXU=0 Radius=0.75
    g3: Circle CenterX=3.36795 CenterY=-47.5 CenterZ=0 NormalX=0 NormalY=0 NormalZ=1 AngleXU=0 Radius=0.75
    g4: LineSegment StartX=-3.36795 StartY=-41.75 StartZ=0 EndX=3.36795 EndY=-41.75 EndZ=0
    g5: LineSegment StartX=3.36795 StartY=-41.75 StartZ=0 EndX=3.36795 EndY=-47.5 EndZ=0
    g6: LineSegment StartX=3.36795 StartY=-47.5 StartZ=0 EndX=-3.36795 EndY=-47.5 EndZ=0
    g7: LineSegment StartX=-3.36795 StartY=-47.5 StartZ=0 EndX=-3.36795 EndY=-41.75 EndZ=0
    g8: LineSegment StartX=3.36795 StartY=-41.75 StartZ=0 EndX=5.1 EndY=-40.75 EndZ=0
    g9: LineSegment StartX=-3.36795 StartY=-41.75 StartZ=0 EndX=-5.1 EndY=-40.75 EndZ=0
    g10: LineSegment StartX=-3.36795 StartY=-47.5 StartZ=0 EndX=-5.1 EndY=-48.5 EndZ=0
    g11: LineSegment StartX=3.36795 StartY=-47.5 StartZ=0 EndX=5.1 EndY=-48.5 EndZ=0
  constraints (27):
    c: Coincident(g4,g5)
    c: Coincident(g5,g6)
    c: Coincident(g6,g7)
    c: Coincident(g7,g4)
    c: Horizontal(g6)
    c: Vertical(g5)
    c: Symmetric(g4,g4,g-2)
    c: Coincident(g8,g4)
    c: Coincident(g8,g-6)
    c: Coincident(g9,g4)
    c: Coincident(g9,g-5)
    c: Coincident(g10,g6)
    c: Coincident(g10,g-5)
    c: Coincident(g11,g5)
    c: Coincident(g11,g-6)
    c: Equal(g8,g11)
    c: Equal(g11,g10)
    c: Coincident(g1,g4)
    c: Coincident(g0,g4)
    c: Coincident(g2,g6)
    c: Coincident(g3,g5)
    c: Equal(g0,g1)
    c: Equal(g1,g3)
    c: Equal(g3,g2)
    c: Diameter(g0) = 1.5
    c: Angle(g4,g9) = 2.61799
    c: Distance(g8) = 2
FEATURE [PartDesign::Pocket] Pocket008  label="Agujeros_paracaidas"
  BaseFeature = -> Pocket005
  Length = 0
  Length2 = 100
  Placement = pos=(0,-4.5,-1e-15) rot=(0,0,1;0rad)
  Profile = -> Sketch017
  Type = 3
  UpToFace = -> Pocket005 [Face32]
FEATURE [Sketcher::SketchObject] Sketch019  label="SK_Agujeros_paracaidas_2"
  ExternalGeometry = -> [Pocket008]
  FullyConstrained = true
  MapMode = 5
  Placement = pos=(0,-53,-3.74e-14) rot=(0,0.707107,0.707107;3.14159rad)
  Support = -> [Pocket008]
  expr: Constraints[6] = 2 * 1.5 + 3 * <<Datos>>.tolerancia
  sketch-geometry (6):
    g0: LineSegment StartX=5.1 StartY=14.677 StartZ=0 EndX=29.5565 EndY=14.677 EndZ=0
    g1: ArcOfCircle CenterX=0 CenterY=0 CenterZ=0 NormalX=0 NormalY=0 NormalZ=1 AngleXU=0 Radius=33 StartAngle=0.473254 EndAngle=0.506517
    g2: LineSegment StartX=25.3565 StartY=16.0094 StartZ=0 EndX=25.3565 EndY=14.677 EndZ=0
    g3: LineSegment StartX=25.3565 StartY=14.677 StartZ=0 EndX=29.1504 EndY=14.677 EndZ=0
    g4: ArcOfCircle CenterX=29.1504 CenterY=14.927 CenterZ=0 NormalX=0 NormalY=0 NormalZ=1 AngleXU=0 Radius=0.25 StartAngle=4.71239 EndAngle=6.75644
    g5: LineSegment StartX=25.3565 StartY=16.0094 StartZ=0 EndX=28.8565 EndY=16.0094 EndZ=0
  constraints (17):
    c: Coincident(g0,g-4)
    c: PointOnObject(g0,g-3)
    c: Horizontal(g0)
    c: Coincident(g1,g-1)
    c: Vertical(g2)
    c: PointOnObject(g3,g0)
    c: DistanceX(g2,g0) = 4.2
    c: Tangent(g1,g4) = -1.5708
    c: Tangent(g3,g4) = -1.5708
    c: PointOnObject(g3,g0)
    c: PointOnObject(g1,g-3)
    c: Horizontal(g5)
    c: Coincident(g2,g5)
    c: Coincident(g1,g5)
    c: DistanceX(g5,g5) = 3.5
    c: Coincident(g2,g3)
    c: Diameter(g4) = 0.5
FEATURE [PartDesign::Pad] Pad008  label="Pieza_agujeros_paracaidas_lateral"
  BaseFeature = -> Pocket008
  Direction = (1,1,1)
  Length = 5
  Length2 = 100
  Placement = pos=(0,-4.5,-1e-15) rot=(0,0,1;0rad)
  Profile = -> Sketch019
  Type = 0
FEATURE [Sketcher::SketchObject] Sketch020  label="agujeros_laterales_paracaidas_SK"
  ExternalGeometry = -> [Pad008]
  FullyConstrained = true
  MapMode = 5
  Placement = pos=(0,-4.5,16.0094) rot=(0,0,1;0rad)
  Support = -> [Pad008]
  sketch-geometry (6):
    g0: LineSegment StartX=-27.1065 StartY=-43.5 StartZ=0 EndX=-27.1065 EndY=-48.5 EndZ=0
    g1: LineSegment StartX=-28.8565 StartY=-43.5 StartZ=0 EndX=-25.3565 EndY=-48.5 EndZ=0
    g2: LineSegment StartX=-25.3565 StartY=-43.5 StartZ=0 EndX=-28.8565 EndY=-48.5 EndZ=0
    g3: GeomPoint X=-27.1065 Y=-46 Z=0
    g4: Circle CenterX=-27.8565 CenterY=-44.9286 CenterZ=0 NormalX=0 NormalY=0 NormalZ=1 AngleXU=0 Radius=0.75
    g5: Circle CenterX=-26.3565 CenterY=-47.0714 CenterZ=0 NormalX=0 NormalY=0 NormalZ=1 AngleXU=0 Radius=0.75
  constraints (16):
    c: PointOnObject(g0,g-3)
    c: PointOnObject(g0,g-6)
    c: Vertical(g0)
    c: Coincident(g1,g-5)
    c: Coincident(g1,g-4)
    c: Coincident(g2,g-4)
    c: Coincident(g2,g-6)
    c: PointOnObject(g3,g2)
    c: PointOnObject(g3,g1)
    c: PointOnObject(g3,g0)
    c: PointOnObject(g4,g1)
    c: Diameter(g4) = 1.5
    c: PointOnObject(g5,g1)
    c: Equal(g4,g5)
    c: Tangent(g5,g0)
    c: Tangent(g4,g0)
FEATURE [PartDesign::Pocket] Pocket009  label="Lateral_paracaidas"
  BaseFeature = -> Pad008
  Length = 5
  Length2 = 100
  Placement = pos=(0,-4.5,-1e-15) rot=(0,0,1;0rad)
  Profile = -> Sketch020
  Type = 2
FEATURE [PartDesign::Mirrored] Mirrored  label="Pieza_lateral_A"
  BaseFeature = -> Pocket009
  MirrorPlane = -> Sketch019 [V_Axis]
  Originals = -> [Pad008]
  Placement = pos=(0,-4.5,-1e-15) rot=(0,0,1;0rad)
FEATURE [PartDesign::Mirrored] Mirrored001  label="Pieza_lateral_B"
  BaseFeature = -> Mirrored
  MirrorPlane = -> Sketch020 [V_Axis]
  Originals = -> [Pocket009]
  Placement = pos=(0,-4.5,-1e-15) rot=(0,0,1;0rad)
FEATURE [PartDesign::Fillet] Fillet
  Base = -> Mirrored001 [Edge55,Edge54,Edge59,Edge58]
  BaseFeature = -> Mirrored001
  Placement = pos=(0,-4.5,-1e-15) rot=(0,0,1;0rad)
  Radius = 0.5
  SupportTransform = false
FEATURE [PartDesign::Fillet] Fillet001
  Base = -> Fillet [Edge40,Edge104,Edge32,Edge96]
  BaseFeature = -> Fillet
  Placement = pos=(0,-4.5,-1e-15) rot=(0,0,1;0rad)
  Radius = 0.5
  SupportTransform = false
FEATURE [PartDesign::Fillet] Fillet002
  Base = -> Fillet001 [Edge38,Edge42]
  BaseFeature = -> Fillet001
  Placement = pos=(0,-4.5,-1e-15) rot=(0,0,1;0rad)
  Radius = 3
  SupportTransform = false
FEATURE [PartDesign::Body] Body001  label="LateralA"
  Group = -> [ShapeBinder,Sketch002,Pad002,Sketch003,Pad003,Sketch007,Pocket,Sketch008,Pocket001,Sketch010,Pocket003,Sketch011,Pocket004,Sketch012,Pad007,Sketch013,Pocket005,Sketch017,Pocket008,Sketch019,Pad008,Sketch020,Pocket009,Mirrored,Mirrored001,Fillet,Fillet001,Fillet002]
  Origin = -> Origin001
  Tip = -> Fillet002
FEATURE [Sketcher::SketchObject] Sketch021  label="Agujeros_sacar_camara_SK"
  ExternalGeometry = -> [Pocket007]
  FullyConstrained = true
  MapMode = 5
  Placement = pos=(-1.1e-15,33,-8) rot=(0,0,1;0rad)
  Support = -> [Pocket007]
  expr: Constraints[29] = (6 + <<Datos>>.tolerancia) / 2
  expr: Constraints[30] = 8 + <<Datos>>.tolerancia
  sketch-geometry (17):
    g0: LineSegment StartX=-32.0156 StartY=12.25 StartZ=0 EndX=32.0156 EndY=12.25 EndZ=0
    g1: LineSegment StartX=-16.5992 StartY=15.4215 StartZ=0 EndX=-11.0923 EndY=9.07851 EndZ=0
    g2: LineSegment StartX=11.0923 StartY=15.4215 StartZ=0 EndX=16.5992 EndY=9.07851 EndZ=0
    g3: ArcOfCircle CenterX=-16.5992 CenterY=15.4215 CenterZ=0 NormalX=0 NormalY=0 NormalZ=1 AngleXU=0 Radius=3.2 StartAngle=0.714964 EndAngle=3.85656
    g4: ArcOfCircle CenterX=-11.0923 CenterY=9.07851 CenterZ=0 NormalX=0 NormalY=0 NormalZ=1 AngleXU=0 Radius=3.2 StartAngle=3.85656 EndAngle=6.99815
    g5: LineSegment StartX=-19.0156 StartY=13.3236 StartZ=0 EndX=-13.5087 EndY=6.98062 EndZ=0
    g6: LineSegment StartX=-14.1829 StartY=17.5194 StartZ=0 EndX=-8.67592 EndY=11.1764 EndZ=0
    g7: ArcOfCircle CenterX=11.0923 CenterY=15.4215 CenterZ=0 NormalX=0 NormalY=0 NormalZ=1 AngleXU=0 Radius=3.2 StartAngle=0.714964 EndAngle=3.85656
    g8: ArcOfCircle CenterX=16.5992 CenterY=9.07851 CenterZ=0 NormalX=0 NormalY=0 NormalZ=1 AngleXU=0 Radius=3.2 StartAngle=3.85656 EndAngle=6.99815
    g9: LineSegment StartX=8.67592 StartY=13.3236 StartZ=0 EndX=14.1829 EndY=6.98062 EndZ=0
    g10: LineSegment StartX=13.5087 StartY=17.5194 StartZ=0 EndX=19.0156 EndY=11.1764 EndZ=0
    g11: LineSegment StartX=-16.5992 StartY=15.4215 StartZ=0 EndX=11.0923 EndY=15.4215 EndZ=0
    g12: LineSegment StartX=-11.0923 StartY=9.07851 StartZ=0 EndX=16.5992 EndY=9.07851 EndZ=0
    g13: GeomPoint X=-13.8458 Y=12.25 Z=0
    g14: GeomPoint X=13.8458 Y=12.25 Z=0
    g15: GeomPoint X=0 Y=15.4215 Z=0
    g16: GeomPoint X=0 Y=9.07851 Z=0
  constraints (37):
    c: PointOnObject(g0,g-3)
    c: Horizontal(g0)
    c: Symmetric(g-4,g-5,g0)
    c: Tangent(g3,g6) = 1.5708
    c: Tangent(g3,g5) = -1.5708
    c: Tangent(g5,g4) = -1.5708
    c: Tangent(g6,g4) = 1.5708
    c: Equal(g3,g4)
    c: Coincident(g3,g1)
    c: Coincident(g4,g1)
    c: Tangent(g7,g10) = 1.5708
    c: Tangent(g7,g9) = -1.5708
    c: Tangent(g9,g8) = -1.5708
    c: Tangent(g10,g8) = 1.5708
    c: Equal(g7,g8)
    c: Coincident(g7,g2)
    c: Coincident(g2,g8)
    c: Coincident(g11,g3)
    c: Coincident(g11,g7)
    c: Coincident(g12,g4)
    c: Coincident(g12,g8)
    c: Horizontal(g12)
    c: Equal(g12,g11)
    c: Equal(g4,g8)
    c: Horizontal(g11)
    c: PointOnObject(g13,g0)
    c: PointOnObject(g14,g2)
    c: PointOnObject(g13,g1)
    c: Symmetric(g13,g14,g-2)
    c: Radius(g7) = 3.2
    c: Distance(g10) = 8.4
    c: PointOnObject(g15,g11)
    c: PointOnObject(g16,g12)
    c: PointOnObject(g16,g-2)
    c: Symmetric(g15,g16,g0)
    c: DistanceX(g3,g-5) = -13
    c: DistanceY(g3,g-5) = -8.8236
FEATURE [PartDesign::Pocket] Pocket010  label="Agujeros_sacar_piezas"
  BaseFeature = -> Pocket007
  Length = 5
  Length2 = 100
  Placement = pos=(0,33,7e-15) rot=(0,0,1;0rad)
  Profile = -> Sketch021
  Type = 2
FEATURE [PartDesign::Mirrored] Mirrored002  label="Ranuras_sujetar_placa"
  BaseFeature = -> Pocket010
  MirrorPlane = -> XZ_Plane002
  Originals = -> [Pad007]
  Placement = pos=(0,33,7e-15) rot=(0,0,1;0rad)
FEATURE [PartDesign::Mirrored] Mirrored003  label="Ranuras_sujetar_placa_2"
  BaseFeature = -> Mirrored002
  MirrorPlane = -> XZ_Plane002
  Originals = -> [Pocket005]
  Placement = pos=(0,33,7e-15) rot=(0,0,1;0rad)
FEATURE [PartDesign::Mirrored] Mirrored004  label="Con_agujeros_superiores"
  BaseFeature = -> Mirrored003
  MirrorPlane = -> XZ_Plane002
  Originals = -> [Pocket008]
  Placement = pos=(0,33,7e-15) rot=(0,0,1;0rad)
FEATURE [PartDesign::MultiTransform] MultiTransform  label="Piezas_agujeros_laterales"
  BaseFeature = -> Mirrored004
  Placement = pos=(0,33,7e-15) rot=(0,0,1;0rad)
FEATURE [PartDesign::MultiTransform] MultiTransform001  label="Parte_lateral"
  BaseFeature = -> Mirrored004
  Originals = -> [Pocket009]
  Placement = pos=(0,33,7e-15) rot=(0,0,1;0rad)
FEATURE [PartDesign::Mirrored] Mirrored005
  MirrorPlane = -> XZ_Plane002
  Placement = pos=(0,33,7e-15) rot=(0,0,1;0rad)
FEATURE [PartDesign::Mirrored] Mirrored006
  MirrorPlane = -> Sketch020 [V_Axis]
  Placement = pos=(0,33,7e-15) rot=(0,0,1;0rad)
FEATURE [PartDesign::MultiTransform] MultiTransform002  label="Parte_lateral_con_agujeros"
  BaseFeature = -> MultiTransform001
  Originals = -> [Pocket009]
  Placement = pos=(0,33,7e-15) rot=(0,0,1;0rad)
  Transformations = -> [Mirrored005,Mirrored006]
FEATURE [PartDesign::Fillet] Fillet003
  Base = -> MultiTransform002 [Edge69,Edge66,Edge73,Edge70]
  BaseFeature = -> MultiTransform002
  Placement = pos=(0,33,7e-15) rot=(0,0,1;0rad)
  Radius = 0.5
  SupportTransform = false
FEATURE [PartDesign::Fillet] Fillet004
  Base = -> Fillet003 [Edge32,Edge92,Edge100,Edge40]
  BaseFeature = -> Fillet003
  Placement = pos=(0,33,7e-15) rot=(0,0,1;0rad)
  Radius = 0.5
  SupportTransform = false
FEATURE [PartDesign::Fillet] Fillet005
  Base = -> Fillet004 [Edge43,Edge39]
  BaseFeature = -> Fillet004
  Placement = pos=(0,33,7e-15) rot=(0,0,1;0rad)
  Radius = 3
  SupportTransform = false
FEATURE [PartDesign::Body] Body002  label="LateralB"
  Group = -> [ShapeBinder001,Sketch004,Pad004,Sketch005,Pad005,Sketch006,Pad006,ShapeBinder002,Sketch009,Pocket002,Sketch015,Pocket007,Sketch021,Pocket010,Mirrored002,Mirrored003,Mirrored004,MultiTransform,MultiTransform001,MultiTransform002,Mirrored005,Mirrored006,Fillet003,Fillet004,Fillet005]
  Origin = -> Origin002
  Tip = -> Fillet005
FEATURE [TechDraw::DrawViewPart] View
  CoarseView = false
  Direction = (1,0,0)
  Focus = 100
  HardHidden = false
  IsoCount = 0
  IsoHidden = false
  IsoVisible = false
  LockPosition = true
  Perspective = false
  Rotation = 0
  Scale = 1.8
  ScaleType = 0
  SeamHidden = false
  SeamVisible = false
  SmoothHidden = false
  SmoothVisible = false
  Source = -> [Body,Body001,Body002]
  X = 150.151
  XDirection = (0,1,0)
  Y = 126.132
FEATURE [TechDraw::DrawViewDimension] Dimension
  Arbitrary = false
  ArbitraryTolerances = false
  EqualTolerance = true
  FormatSpec = %.2f
  FormatSpecOverTolerance = %+.2f
  FormatSpecUnderTolerance = %+.2f
  Inverted = false
  LockPosition = false
  MeasureType = 1
  OverTolerance = 0
  References2D = -> [View]
  Rotation = 0
  ScaleType = 0
  TheoreticalExact = false
  Type = 1
  UnderTolerance = 0
  X = 5.68e-14
  Y = -59.4
FEATURE [TechDraw::DrawPage] Page
  KeepUpdated = true
  NextBalloonIndex = 1
  ProjectionType = 0
  Template = -> Template
  Views = -> [View,Dimension]
FEATURE [PartDesign::ShapeBinder] ShapeBinder003
  Placement = pos=(0,-4.5,-1e-15) rot=(0,0,1;0rad)
  Support = -> [Fillet002]
  TraceSupport = false
FEATURE [Sketcher::SketchObject] Sketch022  label="Sketch_placa"
  ExternalGeometry = -> [ShapeBinder003]
  FullyConstrained = false
  Placement = pos=(0,0,-3.74e-14) rot=(0,0.707107,0.707107;3.14159rad)
  Support = -> [ShapeBinder003]
  expr: Constraints[8] = <<Datos>>.anchoPlaca
  sketch-geometry (5):
    g0: LineSegment StartX=-1.5 StartY=31.7351 StartZ=0 EndX=1.5 EndY=31.7351 EndZ=0
    g1: LineSegment StartX=1.5 StartY=31.7351 StartZ=0 EndX=1.5 EndY=-5 EndZ=0
    g2: LineSegment StartX=1.5 StartY=-5 StartZ=0 EndX=-1.5 EndY=-5 EndZ=0
    g3: LineSegment StartX=-1.5 StartY=-5 StartZ=0 EndX=-1.5 EndY=31.7351 EndZ=0
    g4: LineSegment StartX=1.5 StartY=-5 StartZ=0 EndX=1.5 EndY=-8 EndZ=0
  constraints (13):
    c: Coincident(g0,g1)
    c: Coincident(g1,g2)
    c: Coincident(g2,g3)
    c: Coincident(g3,g0)
    c: Horizontal(g2)
    c: Vertical(g1)
    c: Vertical(g3)
    c: Symmetric(g0,g0,g-2)
    c: DistanceX(g0,g0) = 3
    c: Coincident(g4,g1)
    c: PointOnObject(g4,g-3)
    c: Vertical(g4)
    c: DistanceY(g4,g4) = 3
FEATURE [PartDesign::Pad] Pad009  label="Placa_electrónica"
  Direction = (1,1,1)
  Length = 104
  Length2 = 100
  Midplane = true
  Placement = pos=(0,-4.5,-1e-15) rot=(0,0,1;0rad)
  Profile = -> Sketch022
  Type = 0
FEATURE [Sketcher::SketchObject] Sketch023
  ExternalGeometry = -> [Pad009]
  FullyConstrained = true
  MapMode = 5
  Placement = pos=(-4.1e-15,-52,3.59e-14) rot=(1,0,0;1.5708rad)
  Support = -> [Pad009]
  sketch-geometry (4):
    g0: LineSegment StartX=-1.5 StartY=-5 StartZ=0 EndX=1.5 EndY=-5 EndZ=0
    g1: LineSegment StartX=1.5 StartY=-5 StartZ=0 EndX=1.5 EndY=14.3 EndZ=0
    g2: LineSegment StartX=1.5 StartY=14.3 StartZ=0 EndX=-1.5 EndY=14.3 EndZ=0
    g3: LineSegment StartX=-1.5 StartY=14.3 StartZ=0 EndX=-1.5 EndY=-5 EndZ=0
  constraints (11):
    c: Coincident(g0,g1)
    c: Coincident(g1,g2)
    c: Coincident(g2,g3)
    c: Coincident(g3,g0)
    c: Horizontal(g0)
    c: Horizontal(g2)
    c: Vertical(g1)
    c: Vertical(g3)
    c: Coincident(g0,g-3)
    c: PointOnObject(g1,g-4)
    c: DistanceY(g1,g1) = 19.3
FEATURE [PartDesign::Pocket] Pocket011
  BaseFeature = -> Pad009
  Length = 4
  Length2 = 100
  Placement = pos=(0,-4.5,-1e-15) rot=(0,0,1;0rad)
  Profile = -> Sketch023
  Type = 0
FEATURE [PartDesign::Body] Body003  label="Placa_electronica"
  Group = -> [ShapeBinder003,Sketch022,Pad009,Sketch023,Pocket011]
  Origin = -> Origin003
  Tip = -> Pocket011
